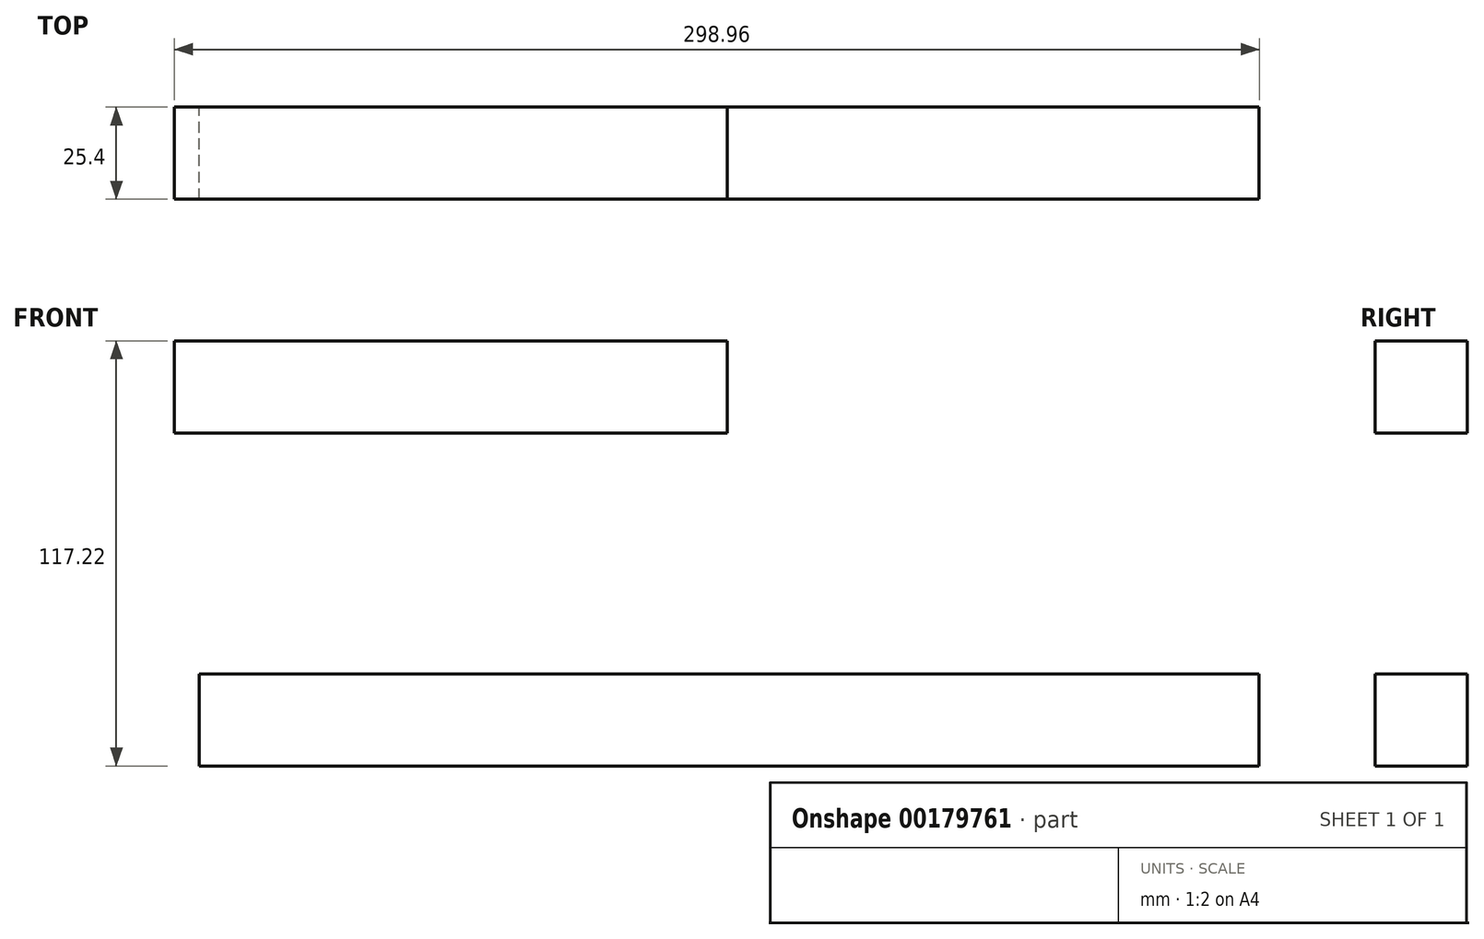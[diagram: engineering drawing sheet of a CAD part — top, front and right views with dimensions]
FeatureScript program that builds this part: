
annotation { "Feature Type Name" : "Feature", "Feature Type Description" : "" }
export const myFeature = defineFeature(function(context is Context, id is Id, definition is map)
    precondition{}
    {
        {
            var Q0;
            Q0=qCreatedBy(makeId("Front.planeOp"),FACE);
            var sketch = newSketch(context, id + "F0", { "sketchPlane" : qUnion([Q0])});
            skLineSegment(sketch, "E0.bottom", {"start": v(-76.57, 52.6) * mm, "end": v(75.83, 52.6) * mm});
            skLineSegment(sketch, "E0.top", {"start": v(-76.57, 27.2) * mm, "end": v(75.83, 27.2) * mm});
            skLineSegment(sketch, "E0.left", {"start": v(-76.57, 52.6) * mm, "end": v(-76.57, 27.2) * mm});
            skLineSegment(sketch, "E0.right", {"start": v(75.83, 52.6) * mm, "end": v(75.83, 27.2) * mm});
            skLineSegment(sketch, "E1.bottom", {"start": v(-69.71, -39.23) * mm, "end": v(222.39, -39.23) * mm});
            skLineSegment(sketch, "E1.top", {"start": v(-69.71, -64.63) * mm, "end": v(222.39, -64.63) * mm});
            skLineSegment(sketch, "E1.left", {"start": v(-69.71, -39.23) * mm, "end": v(-69.71, -64.63) * mm});
            skLineSegment(sketch, "E1.right", {"start": v(222.39, -39.23) * mm, "end": v(222.39, -64.63) * mm});
            skSolve(sketch);
        }
        {
            var Q0;
            Q0 = qSketchRegion(id + "F0", true);
            extrude(context, id + "F1", {"entities" : qUnion([Q0]), "depth" : 25.4 * mm});
        }
    });
